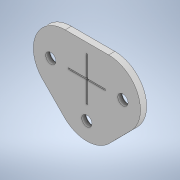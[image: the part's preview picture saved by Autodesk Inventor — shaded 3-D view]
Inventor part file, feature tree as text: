
AUTODESK INVENTOR PART (.ipt)
format: ipt  version: 2021 (Build 250183000, 183)  size: 261,632 bytes
history: native  units: mm
features: extrude x6, sketch x6, projected_geometry x3, mirror x2, chamfer x1, boolean_combine x1, pattern_linear x1, fillet x1
ambient origin geometry x8: Origin, YZ Plane, XZ Plane, XY Plane, X Axis, Y Axis, Z Axis, Center Point
bodies: Solid3 (feature_tree)
feature tree (21):
  extrude  "Extrusion3"  Depth=5.0mm
  extrude  "Extrusion4"  Depth=17.162mm
  chamfer  "Chamfer1"  Distance=1.5mm
  extrude  "Extrusion5"  Depth=21.669147mm
  boolean_combine  "Combine1"
  mirror  "Mirror1"
  mirror  "Mirror2"
  extrude  "Extrusion8"  Depth=21.669147mm
  pattern_linear  "Rectangular Pattern1"  Spacing1=4.0mm  [1 undecoded]
  extrude  "Extrusion6"  Depth=21.669147mm
  fillet  "Fillet1"  Radius=4.0mm
  extrude  "Extrusion7"  Depth=2.0mm TaperAngle=0.0deg
  sketch  "Sketch1"  dims[d0=13.0mm d7=5.0mm]
  sketch  "Sketch4"  dims[d8=5.321mm d9=17.162mm]
  projected_geometry  "Projected Loop1"
  sketch  "Sketch5"  dims[d10=5.321mm]
  sketch  "Sketch6"  dims[d11=5.0mm]
  projected_geometry  "Projected Loop2"
  sketch  "Sketch7"  dims[d12=2.218mm]
  sketch  "Sketch8"  dims[d13=12.0mm d14=1.5mm d15=3.3mm d16=4.0mm d17=4.0mm d18=3.3mm d19=4.0mm d20=2.0mm d21=0.0mm d22=0.4mm d23=0.4mm d24=1.5mm d25=0.0mm d26=0.7mm d27=2.0mm d28=45.0deg d32=1.2mm d33=2.0mm d34=0.0mm d35=0.0mm d36=24.0mm d37=39.0mm d38=20.0mm d40=24.0mm d41=0.25mm d42=1.2mm d43=0.0mm d44=2.0mm d45=0.5mm d46=0.0mm d47=0.4mm d48=0.0mm d49=0.0mm d50=3.3mm d51=30.0mm d52=4.6mm d53=1.5mm d54=21.669147mm d55=5.676247mm]
  projected_geometry  "Projected Loop3"
note: 1 required parameter value undecoded (feature->parameter linkage not recoverable at this tier; creation-order binding heuristic only, values carry confidence <= 0.55)
